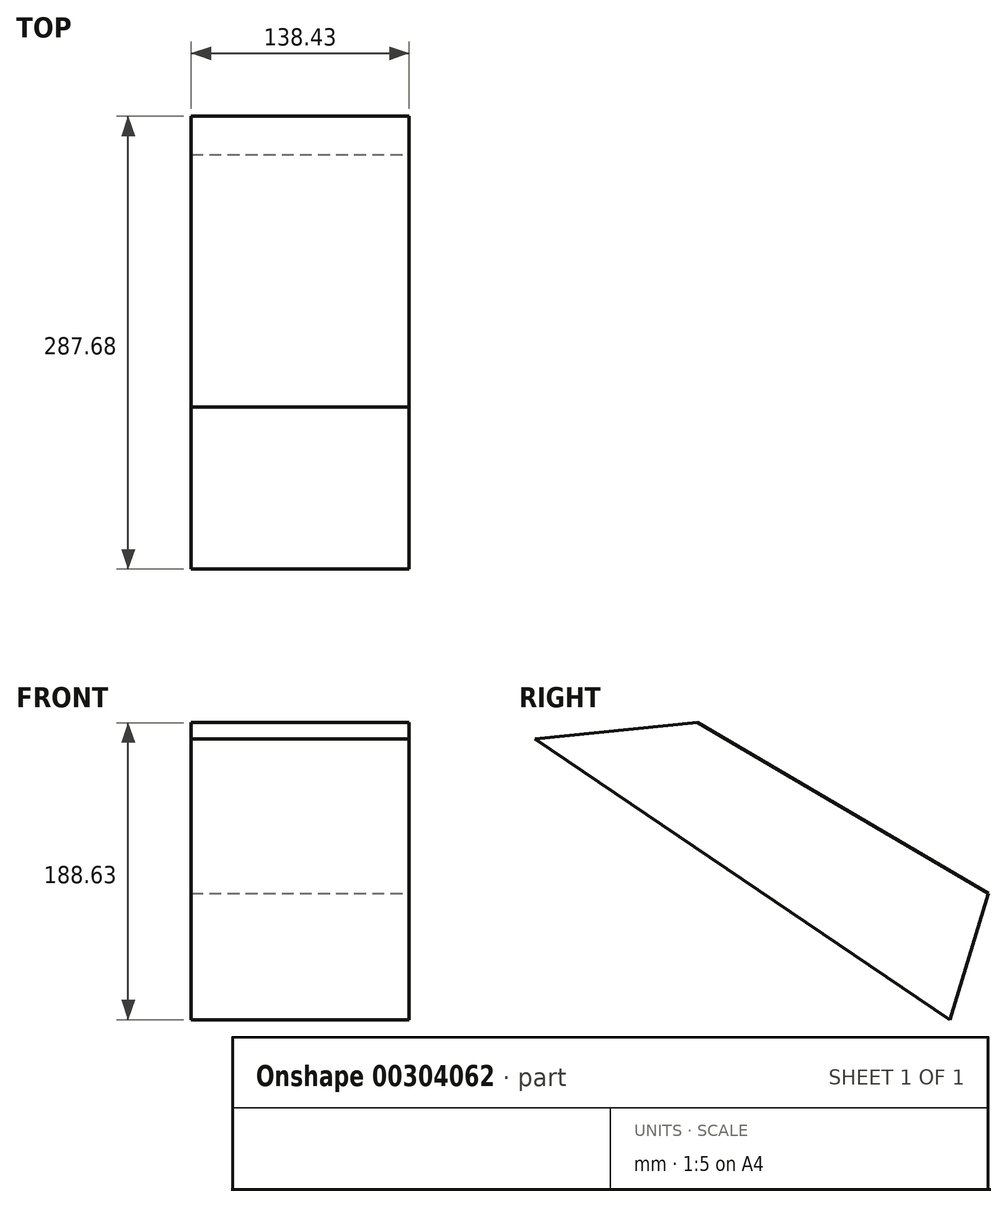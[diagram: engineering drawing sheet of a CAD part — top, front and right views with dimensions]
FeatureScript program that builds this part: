
annotation { "Feature Type Name" : "Feature", "Feature Type Description" : "" }
export const myFeature = defineFeature(function(context is Context, id is Id, definition is map)
    precondition{}
    {
        {
            var Q0;
            Q0=qCreatedBy(makeId("Right.planeOp"),FACE);
            var sketch = newSketch(context, id + "F0", { "sketchPlane" : qUnion([Q0])});
            skLineSegment(sketch, "E0", {"start": v(59.45, 0) * mm, "end": v(162.42, 10.41) * mm});
            skLineSegment(sketch, "E1", {"start": v(162.42, 10.41) * mm, "end": v(347.13, -97.88) * mm});
            skLineSegment(sketch, "E2", {"start": v(347.13, -97.88) * mm, "end": v(322.72, -178.22) * mm});
            skLineSegment(sketch, "E3", {"start": v(322.72, -178.22) * mm, "end": v(59.45, 0) * mm});
            skSolve(sketch);
        }
        {
            var Q0;
            Q0 = qSketchRegion(id + "F0", true);
            extrude(context, id + "F1", {"entities" : qUnion([Q0]), "oppositeDirection" : true, "depth" : 138.43 * mm});
        }
    });
